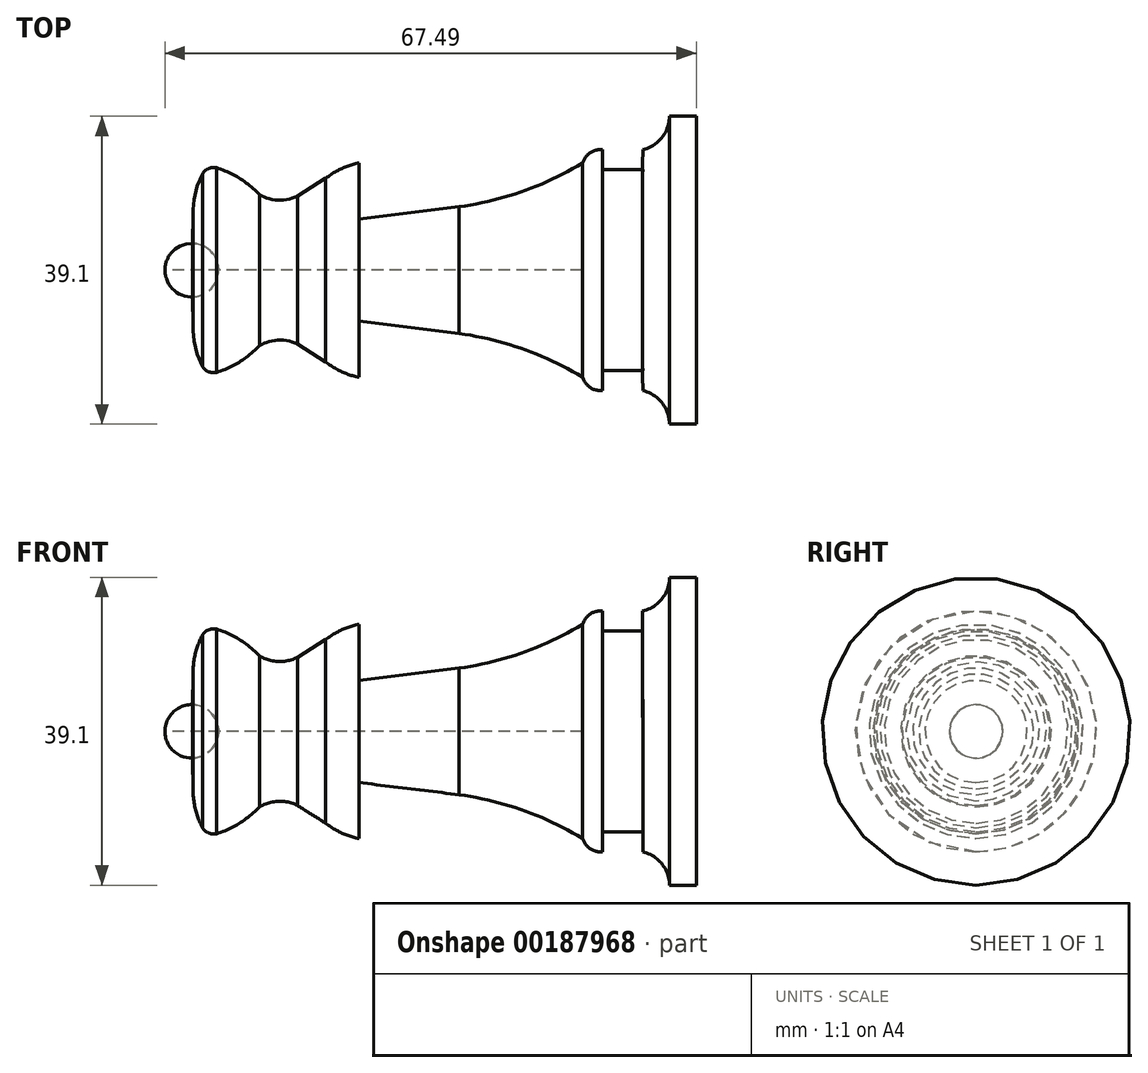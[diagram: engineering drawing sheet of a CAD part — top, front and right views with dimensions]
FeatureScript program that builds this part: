
annotation { "Feature Type Name" : "Feature", "Feature Type Description" : "" }
export const myFeature = defineFeature(function(context is Context, id is Id, definition is map)
    precondition{}
    {
        {
            var Q0;
            Q0=qCreatedBy(makeId("Front.planeOp"),FACE);
            var sketch = newSketch(context, id + "F0", { "sketchPlane" : qUnion([Q0])});
            skPoint(sketch, "E0", {"position": v(-39, 0) * mm});
            skArc(sketch, "E1.trimOffspring", {"start": v(-37.65, 2) * mm, "mid": v(-39.1, 1.43) * mm, "end": v(-39.7, 0) * mm});
            skPoint(sketch, "E2.orphan", {"position": v(-37.5, 0) * mm});
            skPoint(sketch, "E3.start.orphan", {"position": v(-41, 11.5) * mm});
            skLineSegment(sketch, "E4", {"start": v(-25.21, 8) * mm, "end": v(-25.21, 3.82) * mm});
            skLineSegment(sketch, "E5", {"start": v(0, 11.5) * mm, "end": v(-2, 11.5) * mm});
            skLineSegment(sketch, "E6", {"start": v(-4, 9) * mm, "end": v(-4, 7.5) * mm});
            skLineSegment(sketch, "E7", {"start": v(-4, 7.5) * mm, "end": v(-7, 7.5) * mm});
            skLineSegment(sketch, "E8", {"start": v(-7, 7.5) * mm, "end": v(-7, 9) * mm});
            skPoint(sketch, "E9", {"position": v(-2.06, 10.25) * mm});
            skPoint(sketch, "E10", {"position": v(-3.06, 9) * mm});
            skPoint(sketch, "E11", {"position": v(-7.8, 9.03) * mm});
            skLineSegment(sketch, "E12", {"start": v(-8.5, 8) * mm, "end": v(-8.5, 0) * mm});
            skPoint(sketch, "E13.trimOffspring.end.orphan", {"position": v(-8.62, 9.06) * mm});
            skPoint(sketch, "E14.orphan", {"position": v(-2.12, 9) * mm});
            skLineSegment(sketch, "E15", {"start": v(0, 0) * mm, "end": v(0, 11.5) * mm});
            skLineSegment(sketch, "E16", {"start": v(0, 0) * mm, "end": v(-8.5, 0) * mm});
            skLineSegment(sketch, "E17", {"start": v(-8.5, 0) * mm, "end": v(-41, 0) * mm});
            skLineSegment(sketch, "E18", {"start": v(-37.65, 2) * mm, "end": v(-37.65, 2) * mm});
            skLineSegment(sketch, "E19", {"start": v(-41, 11.5) * mm, "end": v(-26.67, 11.5) * mm});
            skPoint(sketch, "E20", {"position": v(-35.84, 7.64) * mm});
            skArc(sketch, "E21", {"start": v(-4, 9) * mm, "mid": v(-2.57, 9.9) * mm, "end": v(-2, 11.5) * mm});
            skArc(sketch, "E22", {"start": v(-7, 9) * mm, "mid": v(-7.93, 8.77) * mm, "end": v(-8.5, 8) * mm});
            skArc(sketch, "E23", {"start": v(-17.7, 4.73) * mm, "mid": v(-12.94, 5.9) * mm, "end": v(-8.5, 8) * mm});
            skLineSegment(sketch, "E24", {"start": v(-25.21, 3.82) * mm, "end": v(-17.71, 4.73) * mm});
            skArc(sketch, "E25", {"start": v(-25.21, 8) * mm, "mid": v(-26.52, 7.58) * mm, "end": v(-27.69, 6.86) * mm});
            skArc(sketch, "E26", {"start": v(-32.62, 5.64) * mm, "mid": v(-31.22, 5.22) * mm, "end": v(-29.8, 5.54) * mm});
            skArc(sketch, "E27", {"start": v(-32.62, 5.64) * mm, "mid": v(-34.1, 6.84) * mm, "end": v(-35.84, 7.64) * mm});
            skArc(sketch, "E28", {"start": v(-35.84, 7.64) * mm, "mid": v(-36.44, 7.59) * mm, "end": v(-36.9, 7.2) * mm});
            skArc(sketch, "E29", {"start": v(-36.9, 7.2) * mm, "mid": v(-37.43, 5.79) * mm, "end": v(-37.6, 4.29) * mm});
            skLineSegment(sketch, "E30", {"start": v(-37.6, 4.29) * mm, "end": v(-37.65, 2) * mm});
            skLineSegment(sketch, "E31", {"start": v(-29.8, 5.54) * mm, "end": v(-27.69, 6.86) * mm});
            skSolve(sketch);
        }
        {
            var Q0;
            Q0=qSketchRegion(id+"F0",true);
            var Q1;
            Q1=sQuery(id+"F0.wireOp",EDGE,"E16");
            revolve(context, id + "F1", {"entities" : qUnion([Q0]), "axis" : qUnion([Q1]), "revolveType" : RevolveType.FULL});
        }
        {
            var Q0;
            Q0=makeQuery(id+"F1.opRevolve","SWEPT_BODY",BODY,{"disambiguationData":[OSD([sQuery(id+"F0.wireOp",EDGE,"3d44b2f9-3c5b-445f-b95f-2f94a00c7f9c"),sQuery(id+"F0.wireOp",EDGE,"E1.trimOffspring"),sQuery(id+"F0.wireOp",EDGE,"b121ef04-23fa-4a38-9f93-d7b6f0e688e5"),sQuery(id+"F0.wireOp",EDGE,"f7d3c5fb-e82c-446d-896c-f5f111a1dbce0.MirrorCS"),sQuery(id+"F0.wireOp",EDGE,"27cb65ef-5ce3-4c83-8abe-4cd599c20872"),sQuery(id+"F0.wireOp",EDGE,"E4"),sQuery(id+"F0.wireOp",EDGE,"E5"),sQuery(id+"F0.wireOp",EDGE,"E6"),sQuery(id+"F0.wireOp",EDGE,"E7"),sQuery(id+"F0.wireOp",EDGE,"E8"),sQuery(id+"F0.wireOp",EDGE,"52f97565-5047-45ac-aa69-9a308e67db17"),sQuery(id+"F0.wireOp",EDGE,"138d7454-4d65-4945-94f0-14ab62864223"),sQuery(id+"F0.wireOp",EDGE,"6056502e-77f8-4cf8-b4c3-37cb1035b5fa"),sQuery(id+"F0.wireOp",EDGE,"E15"),sQuery(id+"F0.wireOp",EDGE,"E16"),sQuery(id+"F0.wireOp",EDGE,"E17"),sQuery(id+"F0.wireOp",EDGE,"E18")])]});
            var Q1;
            Q1=qCreatedBy(makeId("Origin.pointOp"),VERTEX);
            transform(context, id + "F2", {"entities" : qUnion([Q0]), "transformType" : TransformType.SCALE_UNIFORMLY, "scale" : 1.7, "scalePoint" : qUnion([Q1]), "makeCopy" : false});
        }
    });
